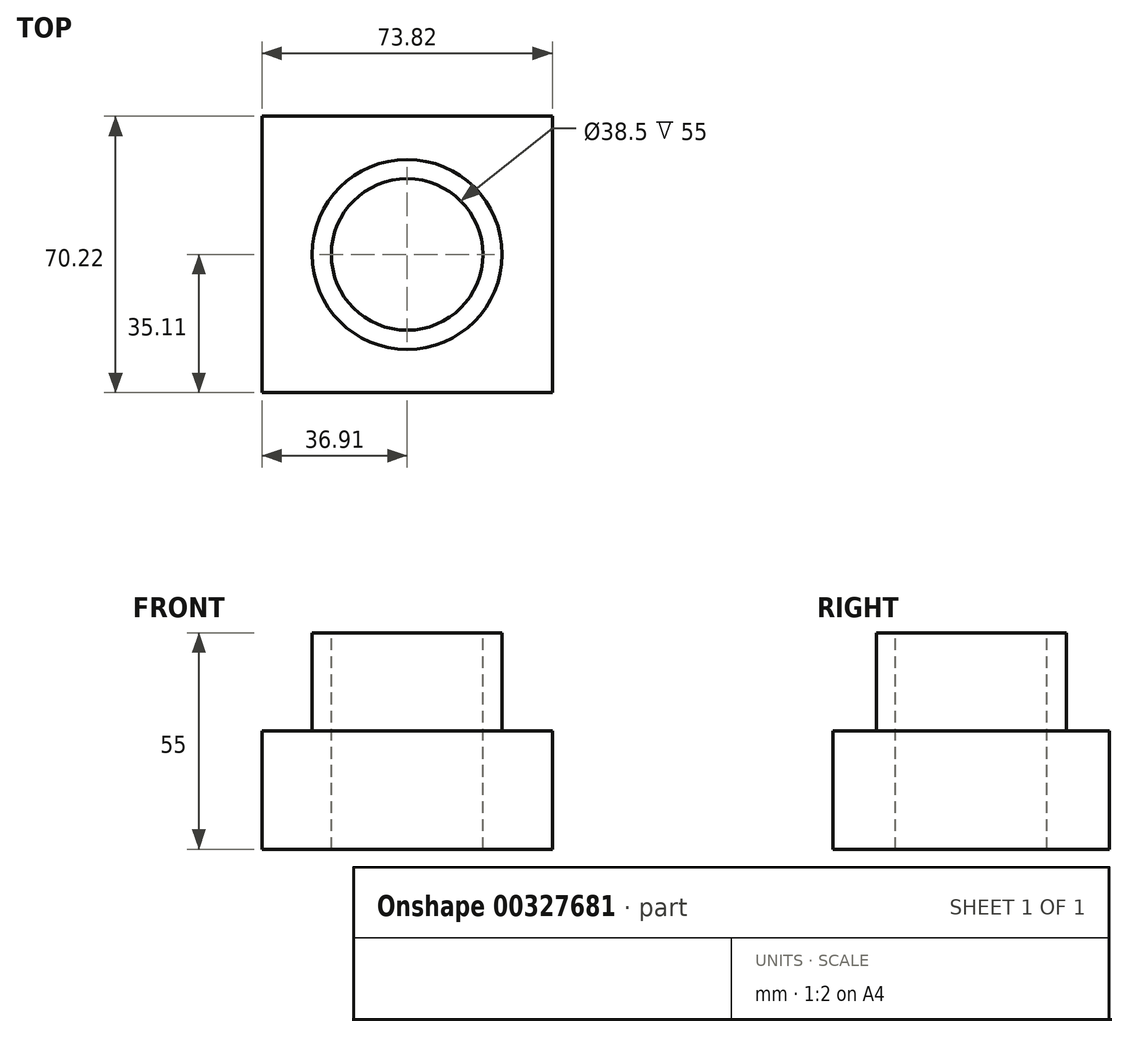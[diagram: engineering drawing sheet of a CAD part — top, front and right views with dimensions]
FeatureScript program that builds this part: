
annotation { "Feature Type Name" : "Feature", "Feature Type Description" : "" }
export const myFeature = defineFeature(function(context is Context, id is Id, definition is map)
    precondition{}
    {
        {
            var Q0;
            Q0=qCreatedBy(makeId("Top.planeOp"),FACE);
            var sketch = newSketch(context, id + "F0", { "sketchPlane" : qUnion([Q0])});
            skLineSegment(sketch, "E0.bottom", {"start": v(36.91, 35.11) * mm, "end": v(-36.91, 35.11) * mm});
            skLineSegment(sketch, "E0.top", {"start": v(36.91, -35.11) * mm, "end": v(-36.91, -35.11) * mm});
            skLineSegment(sketch, "E0.left", {"start": v(36.91, 35.11) * mm, "end": v(36.91, -35.11) * mm});
            skLineSegment(sketch, "E0.right", {"start": v(-36.91, 35.11) * mm, "end": v(-36.91, -35.11) * mm});
            skPoint(sketch, "E0.middle", {"position": v(0, 0) * mm});
            skSolve(sketch);
        }
        {
            var Q0;
            Q0 = qSketchRegion(id + "F0", true);
            extrude(context, id + "F1", {"entities" : qUnion([Q0]), "depth" : 30 * mm});
        }
        {
            var Q0;
            Q0=makeQuery(id+"F1.opExtrude","CAP_FACE",FACE,{"disambiguationData":[OSD([sQuery(id+"F0.wireOp",EDGE,"E0.bottom"),sQuery(id+"F0.wireOp",EDGE,"E0.top"),sQuery(id+"F0.wireOp",EDGE,"E0.left"),sQuery(id+"F0.wireOp",EDGE,"E0.right")])],"isStart":false});
            var sketch = newSketch(context, id + "F2", { "sketchPlane" : qUnion([Q0])});
            skCircle(sketch, "E1", {"center": v(0, 0) * mm, "radius": 19.25 * mm});
            skSolve(sketch);
        }
        {
            var Q0;
            Q0 = qSketchRegion(id + "F2", true);
            extrude(context, id + "F3", {"entities" : qUnion([Q0]), "operationType" : NewBodyOperationType.REMOVE, "endBound" : BoundingType.THROUGH_ALL, "oppositeDirection" : true, "depth" : 25 * mm});
        }
        {
            var Q0;
            Q0=makeQuery(id+"F1.opExtrude","CAP_FACE",FACE,{"disambiguationData":[OSD([sQuery(id+"F0.wireOp",EDGE,"E0.bottom"),sQuery(id+"F0.wireOp",EDGE,"E0.top"),sQuery(id+"F0.wireOp",EDGE,"E0.left"),sQuery(id+"F0.wireOp",EDGE,"E0.right")])],"isStart":false});
            var sketch = newSketch(context, id + "F4", { "sketchPlane" : qUnion([Q0])});
            skCircle(sketch, "E2", {"center": v(0, 0) * mm, "radius": 24.15 * mm});
            skCircle(sketch, "E3.0", {"center": v(0, 0) * mm, "radius": 19.25 * mm});
            skSolve(sketch);
        }
        {
            var Q0;
            Q0 = qSketchRegion(id + "F4", true);
            extrude(context, id + "F5", {"entities" : qUnion([Q0]), "operationType" : NewBodyOperationType.ADD, "depth" : 25 * mm});
        }
    });
